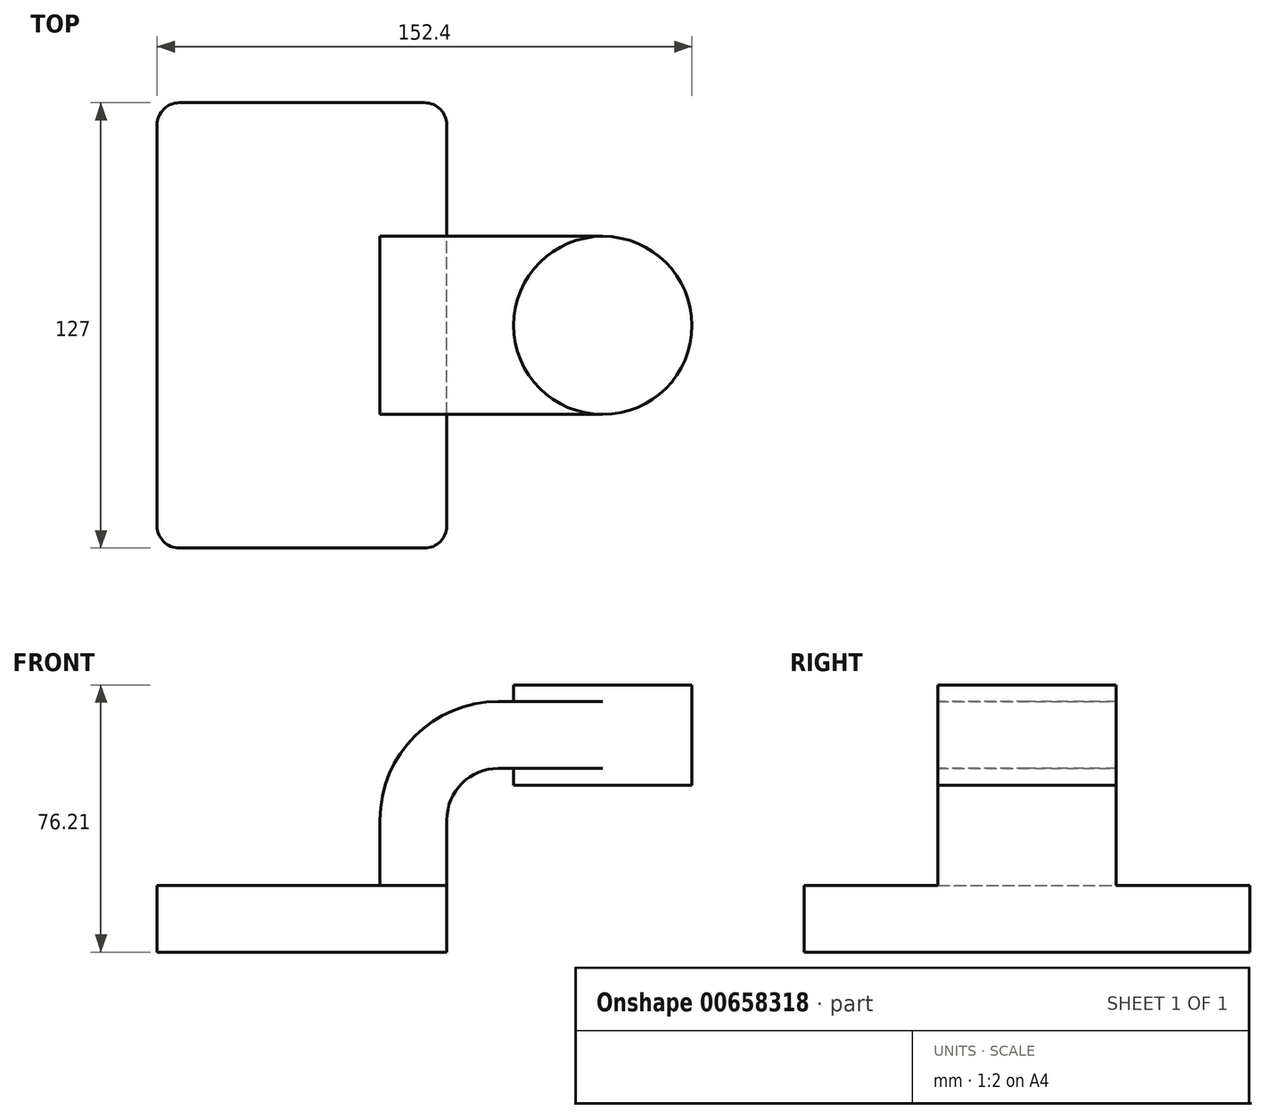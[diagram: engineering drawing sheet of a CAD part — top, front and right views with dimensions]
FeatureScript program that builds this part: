
annotation { "Feature Type Name" : "Feature", "Feature Type Description" : "" }
export const myFeature = defineFeature(function(context is Context, id is Id, definition is map)
    precondition{}
    {
        {
            var Q0;
            Q0=qCreatedBy(makeId("Front.planeOp"),FACE);
            var sketch = newSketch(context, id + "F0", { "sketchPlane" : qUnion([Q0])});
            skLineSegment(sketch, "E0.bottom", {"start": v(-41.28, -9.52) * mm, "end": v(41.28, -9.52) * mm});
            skLineSegment(sketch, "E0.top", {"start": v(-41.28, 9.53) * mm, "end": v(41.28, 9.53) * mm});
            skLineSegment(sketch, "E0.left", {"start": v(-41.27, -9.52) * mm, "end": v(-41.28, 9.53) * mm});
            skLineSegment(sketch, "E0.right", {"start": v(41.28, -9.52) * mm, "end": v(41.28, 9.53) * mm});
            skPoint(sketch, "E0.middle", {"position": v(0, 0) * mm});
            skLineSegment(sketch, "E1.bottom", {"start": v(60.32, 38.1) * mm, "end": v(111.12, 38.1) * mm});
            skLineSegment(sketch, "E1.top", {"start": v(60.32, 66.68) * mm, "end": v(111.12, 66.68) * mm});
            skLineSegment(sketch, "E1.left", {"start": v(60.32, 38.1) * mm, "end": v(60.32, 66.68) * mm});
            skLineSegment(sketch, "E1.right", {"start": v(111.12, 38.1) * mm, "end": v(111.12, 66.68) * mm});
            skPoint(sketch, "E1.middle", {"position": v(85.72, 52.39) * mm});
            skLineSegment(sketch, "E2", {"start": v(41.27, 9.53) * mm, "end": v(41.27, 28.14) * mm});
            skArc(sketch, "E3", {"start": v(41.28, 28.14) * mm, "mid": v(45.6, 38.56) * mm, "end": v(56.01, 42.88) * mm});
            skLineSegment(sketch, "E4", {"start": v(56.01, 42.88) * mm, "end": v(85.72, 42.88) * mm});
            skLineSegment(sketch, "E5.0", {"start": v(56.01, 61.93) * mm, "end": v(85.72, 61.93) * mm});
            skArc(sketch, "E5.1", {"start": v(22.23, 28.14) * mm, "mid": v(32.12, 52.03) * mm, "end": v(56.01, 61.93) * mm});
            skLineSegment(sketch, "E5.2", {"start": v(22.22, 9.53) * mm, "end": v(22.22, 28.14) * mm});
            skLineSegment(sketch, "E6", {"start": v(85.72, 38.1) * mm, "end": v(85.72, 66.68) * mm});
            skFitSpline(sketch, "E7", {"points": [v(-41.27, 9.53) * mm, v(56.01, 61.93) * mm], "startDerivative": vector(0.74, 61.1) * mm, "endDerivative": vector(108.33, -0.27) * mm});
            skSolve(sketch);
        }
        {
            var Q0;
            Q0=makeQuery(id+"F0.imprint","IMPRINT",FACE,{"disambiguationData":[TD([[makeQuery(id+"F0.imprint","IMPRINT",EDGE,{"derivedFrom":sQuery(id+"F0.wireOp",EDGE,"E0.bottom")}),1.0]])]});
            extrude(context, id + "F1", {"entities" : qUnion([Q0]), "endBound" : BoundingType.SYMMETRIC, "depth" : 127 * mm, "offsetDistance" : 25.4 * mm});
        }
        {
            var Q0;
            {var subQ1=sQuery(id+"F0.wireOp",EDGE,"E2");Q0=makeQuery(id+"F0.imprint","IMPRINT",FACE,{"disambiguationData":[TD([[makeQuery(id+"F0.imprint","IMPRINT",EDGE,{"derivedFrom":subQ1}),1.0]])]});}
            var Q1;
            {var subQ0=sQuery(id+"F0.wireOp",EDGE,"E4");var subQ1=sQuery(id+"F0.wireOp",EDGE,"E1.left");var subQ2=makeQuery(id+"F0.imprint","INTERSECT",VERTEX,{"derivedFrom":[subQ1,subQ0]});Q1=makeQuery(id+"F0.imprint","IMPRINT",FACE,{"disambiguationData":[TD([[makeQuery(id+"F0.imprint","IMPRINT",EDGE,{"disambiguationData":[TD([[subQ2,-1.0]])],"derivedFrom":subQ1}),-1.0]])]});}
            extrude(context, id + "F2", {"entities" : qUnion([Q0, Q1]), "operationType" : NewBodyOperationType.ADD, "endBound" : BoundingType.SYMMETRIC, "depth" : 50.8 * mm, "offsetDistance" : 25.4 * mm});
        }
        {
            var Q0;
            Q0=makeQuery(id+"F0.imprint","IMPRINT",FACE,{"disambiguationData":[TD([[makeQuery(id+"F0.imprint","IMPRINT",EDGE,{"derivedFrom":sQuery(id+"F0.wireOp",EDGE,"E5.1")}),1.0]])]});
            extrude(context, id + "F3", {"entities" : qUnion([Q0]), "operationType" : NewBodyOperationType.ADD, "endBound" : BoundingType.SYMMETRIC, "depth" : 15.88 * mm, "offsetDistance" : 25.4 * mm});
        }
        {
            var Q0;
            {var subQ0=sQuery(id+"F0.wireOp",EDGE,"E1.right");Q0=makeQuery(id+"F0.imprint","IMPRINT",FACE,{"disambiguationData":[TD([[makeQuery(id+"F0.imprint","IMPRINT",EDGE,{"derivedFrom":subQ0}),1.0]])]});}
            var Q1;
            Q1=sQuery(id+"F0.wireOp",EDGE,"E6");
            revolve(context, id + "F4", {"operationType" : NewBodyOperationType.ADD, "entities" : qUnion([Q0]), "axis" : qUnion([Q1]), "revolveType" : RevolveType.FULL});
        }
        {
            var Q0;
            Q0=makeQuery(id+"F1.opExtrude","CAP_EDGE",EDGE,{"disambiguationData":[OSD([sQuery(id+"F0.wireOp",EDGE,"E0.right")])],"isStart":true});
            var Q1;
            Q1=makeQuery(id+"F1.opExtrude","CAP_EDGE",EDGE,{"disambiguationData":[OSD([sQuery(id+"F0.wireOp",EDGE,"E0.left")])],"isStart":true});
            var Q2;
            Q2=makeQuery(id+"F1.opExtrude","CAP_EDGE",EDGE,{"disambiguationData":[OSD([sQuery(id+"F0.wireOp",EDGE,"E0.right")])],"isStart":false});
            var Q3;
            Q3=makeQuery(id+"F1.opExtrude","CAP_EDGE",EDGE,{"disambiguationData":[OSD([sQuery(id+"F0.wireOp",EDGE,"E0.left")])],"isStart":false});
            fillet(context, id + "F5", {"entities" : qUnion([Q0, Q1, Q2, Q3]), "radius" : 6.35 * mm, "tangentPropagation" : true, "allowEdgeOverflow" : false});
        }
    });
